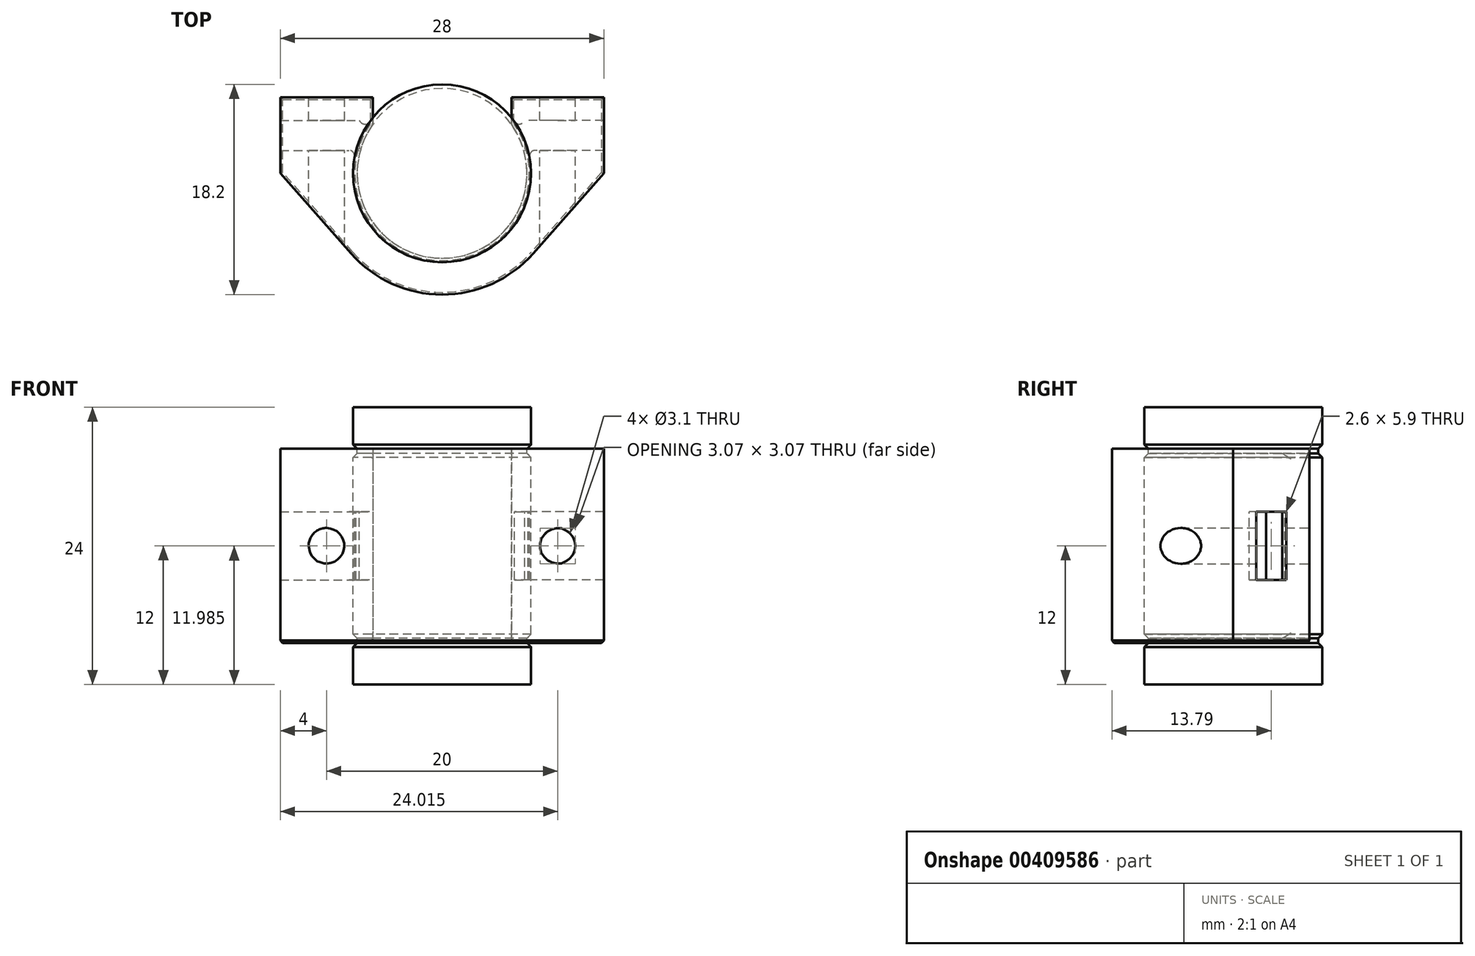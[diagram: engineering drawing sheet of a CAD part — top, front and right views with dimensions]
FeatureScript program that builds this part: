
annotation { "Feature Type Name" : "Feature", "Feature Type Description" : "" }
export const myFeature = defineFeature(function(context is Context, id is Id, definition is map)
    precondition{}
    {
        {
            var Q0;
            Q0=qCreatedBy(makeId("Front.planeOp"),FACE);
            var sketch = newSketch(context, id + "F0", { "sketchPlane" : qUnion([Q0])});
            skLineSegment(sketch, "E0", {"start": v(0, 12) * mm, "end": v(0, -12) * mm});
            skLineSegment(sketch, "E1.bottom", {"start": v(-4, 12) * mm, "end": v(-7.5, 12) * mm});
            skLineSegment(sketch, "E1.top", {"start": v(-4, -12) * mm, "end": v(-7.5, -12) * mm});
            skLineSegment(sketch, "E1.left", {"start": v(-4, 12) * mm, "end": v(-4, -12) * mm, "construction": true});
            skLineSegment(sketch, "E2", {"start": v(-7.5, 12) * mm, "end": v(-7.5, 8.75) * mm, "construction": true});
            skLineSegment(sketch, "E3", {"start": v(-7.5, 8.75) * mm, "end": v(-7.15, 8.75) * mm, "construction": true});
            skLineSegment(sketch, "E4", {"start": v(-7.15, 8.75) * mm, "end": v(-7.15, 7.65) * mm, "construction": true});
            skLineSegment(sketch, "E5", {"start": v(-7.15, 7.65) * mm, "end": v(-7.5, 7.65) * mm, "construction": true});
            skLineSegment(sketch, "E6", {"start": v(-7.5, 7.65) * mm, "end": v(-7.5, 0) * mm, "construction": true});
            skLineSegment(sketch, "E7.MirrorCS", {"start": v(-7.5, -8.75) * mm, "end": v(-7.15, -8.75) * mm, "construction": true});
            skLineSegment(sketch, "E8.MirrorCS", {"start": v(-7.15, -8.75) * mm, "end": v(-7.15, -7.65) * mm, "construction": true});
            skLineSegment(sketch, "E9.MirrorCS", {"start": v(-7.15, -7.65) * mm, "end": v(-7.5, -7.65) * mm, "construction": true});
            skLineSegment(sketch, "E10", {"start": v(-7.5, 0) * mm, "end": v(-7.5, -7.65) * mm, "construction": true});
            skLineSegment(sketch, "E11", {"start": v(-7.5, -8.75) * mm, "end": v(-7.5, -12) * mm, "construction": true});
            skLineSegment(sketch, "E12.0", {"start": v(-7.7, 12) * mm, "end": v(-7.7, 8.75) * mm});
            skLineSegment(sketch, "E13.0", {"start": v(-7.35, 8.75) * mm, "end": v(-7.35, 7.65) * mm});
            skLineSegment(sketch, "E14", {"start": v(-7.7, 8.75) * mm, "end": v(-7.35, 8.4) * mm});
            skLineSegment(sketch, "E15", {"start": v(-7.7, 7.65) * mm, "end": v(-7.7, 0) * mm});
            skLineSegment(sketch, "E16", {"start": v(-7.7, 7.65) * mm, "end": v(-7.35, 8) * mm});
            skLineSegment(sketch, "E17", {"start": v(-7.7, 12) * mm, "end": v(-7.5, 12) * mm});
            skLineSegment(sketch, "E18.MirrorCS", {"start": v(-7.7, -7.65) * mm, "end": v(-7.7, 0) * mm});
            skLineSegment(sketch, "E19.MirrorCS", {"start": v(-7.7, -7.65) * mm, "end": v(-7.35, -8) * mm});
            skLineSegment(sketch, "E20.MirrorCS", {"start": v(-7.35, -8.75) * mm, "end": v(-7.35, -7.65) * mm});
            skLineSegment(sketch, "E21.MirrorCS", {"start": v(-7.7, -8.75) * mm, "end": v(-7.35, -8.4) * mm});
            skLineSegment(sketch, "E22.MirrorCS", {"start": v(-7.7, -12) * mm, "end": v(-7.7, -8.75) * mm});
            skLineSegment(sketch, "E23.MirrorCS", {"start": v(-7.7, -12) * mm, "end": v(-7.5, -12) * mm});
            skLineSegment(sketch, "E24", {"start": v(-4, 12) * mm, "end": v(0, 12) * mm});
            skLineSegment(sketch, "E25", {"start": v(-4, -12) * mm, "end": v(0, -12) * mm});
            skSolve(sketch);
        }
        {
            var Q0;
            Q0=qCreatedBy(makeId("Top.planeOp"),FACE);
            var sketch = newSketch(context, id + "F1", { "sketchPlane" : qUnion([Q0])});
            skLineSegment(sketch, "E26", {"start": v(-5, 6.6) * mm, "end": v(5, 6.6) * mm, "construction": true});
            skCircle(sketch, "E27", {"center": v(0, 0) * mm, "radius": 7.5 * mm, "construction": true});
            skLineSegment(sketch, "E28", {"start": v(5, 6.6) * mm, "end": v(5, 5.6) * mm, "construction": true});
            skLineSegment(sketch, "E29", {"start": v(-5, 6.6) * mm, "end": v(-5, 5.6) * mm, "construction": true});
            skLineSegment(sketch, "E30", {"start": v(-5, 6.6) * mm, "end": v(-10, 6.6) * mm, "construction": true});
            skLineSegment(sketch, "E31", {"start": v(5, 6.6) * mm, "end": v(10, 6.6) * mm, "construction": true});
            skLineSegment(sketch, "E32", {"start": v(-10, 6.6) * mm, "end": v(-10, 4.6) * mm, "construction": true});
            skLineSegment(sketch, "E33.bottom", {"start": v(-12.85, 4.6) * mm, "end": v(-7.15, 4.6) * mm, "construction": true});
            skLineSegment(sketch, "E33.top", {"start": v(-12.85, 2) * mm, "end": v(-7.15, 2) * mm, "construction": true});
            skLineSegment(sketch, "E33.left", {"start": v(-12.85, 4.6) * mm, "end": v(-12.85, 2) * mm, "construction": true});
            skLineSegment(sketch, "E33.right", {"start": v(-7.15, 4.6) * mm, "end": v(-7.15, 2) * mm, "construction": true});
            skSolve(sketch);
        }
        {
            var Q0;
            Q0 = qSketchRegion(id + "F0", true);
            var Q1;
            Q1=sQuery(id+"F0.wireOp",EDGE,"E0");
            revolve(context, id + "F2", {"entities" : qUnion([Q0]), "axis" : qUnion([Q1]), "revolveType" : RevolveType.FULL});
        }
        {
            var Q0;
            Q0=qCreatedBy(makeId("Top.planeOp"),FACE);
            var sketch = newSketch(context, id + "F3", { "sketchPlane" : qUnion([Q0])});
            skPoint(sketch, "E34.0", {"position": v(0, 6.6) * mm});
            skLineSegment(sketch, "E35", {"start": v(0, 6.6) * mm, "end": v(-14, 6.6) * mm, "construction": true});
            skLineSegment(sketch, "E36", {"start": v(-14, 6.6) * mm, "end": v(-14, 0) * mm});
            skLineSegment(sketch, "E37.MirrorCS", {"start": v(0, 6.6) * mm, "end": v(14, 6.6) * mm, "construction": true});
            skLineSegment(sketch, "E38.MirrorCS", {"start": v(14, 6.6) * mm, "end": v(14, 0) * mm});
            skCircle(sketch, "E39.0", {"center": v(0, 0) * mm, "radius": 7.5 * mm, "construction": true});
            skCircle(sketch, "E40.0", {"center": v(0, 0) * mm, "radius": 10.5 * mm, "construction": true});
            skArc(sketch, "E41", {"start": v(-7.88, -6.95) * mm, "mid": v(0, -10.5) * mm, "end": v(7.88, -6.95) * mm});
            skLineSegment(sketch, "E42", {"start": v(-14, 0) * mm, "end": v(-7.87, -6.95) * mm});
            skLineSegment(sketch, "E43.MirrorCS", {"start": v(14, 0) * mm, "end": v(7.87, -6.95) * mm});
            skLineSegment(sketch, "E44.0", {"start": v(-12.85, 4.6) * mm, "end": v(-7.15, 4.6) * mm, "construction": true});
            skLineSegment(sketch, "E45.0", {"start": v(-12.85, 2) * mm, "end": v(-7.15, 2) * mm, "construction": true});
            skLineSegment(sketch, "E46.0", {"start": v(-12.85, 4.6) * mm, "end": v(-12.85, 2) * mm, "construction": true});
            skLineSegment(sketch, "E47", {"start": v(-14, 6.6) * mm, "end": v(-6, 6.6) * mm});
            skLineSegment(sketch, "E48.MirrorCS", {"start": v(14, 6.6) * mm, "end": v(6, 6.6) * mm});
            skLineSegment(sketch, "E49.0", {"start": v(-7.15, 4.6) * mm, "end": v(-7.15, 2) * mm, "construction": true});
            skLineSegment(sketch, "E50", {"start": v(-6, 6.6) * mm, "end": v(-6, 3.3) * mm});
            skPoint(sketch, "E50.endSnap0", {"position": v(-7.15, 3.3) * mm});
            skLineSegment(sketch, "E51", {"start": v(-6, 3.3) * mm, "end": v(0, 3.3) * mm});
            skLineSegment(sketch, "E52.MirrorCS", {"start": v(6, 6.6) * mm, "end": v(6, 3.3) * mm});
            skLineSegment(sketch, "E53.MirrorCS", {"start": v(6, 3.3) * mm, "end": v(0, 3.3) * mm});
            skSolve(sketch);
        }
        {
            var Q0;
            Q0 = qSketchRegion(id + "F3", true);
            var Q1;
            Q1=sQuery(id+"F0.wireOp",VERTEX,"E14.end");
            var Q2;
            Q2=sQuery(id+"F0.wireOp",VERTEX,"E21.MirrorCS.end");
            extrude(context, id + "F4", {"entities" : qUnion([Q0]), "endBound" : BoundingType.UP_TO_VERTEX, "endBoundEntityVertex" : qUnion([Q1]), "depth" : 25 * mm, "hasSecondDirection" : true, "secondDirectionBound" : BoundingType.UP_TO_VERTEX, "secondDirectionOppositeDirection" : true, "secondDirectionBoundEntityVertex" : qUnion([Q2]), "secondDirectionDepth" : 25 * mm});
        }
        {
            var Q0;
            Q0=makeQuery(id+"F4.opExtrude","SWEPT_FACE",FACE,{"disambiguationData":[OSD([sQuery(id+"F3.wireOp",EDGE,"E48.MirrorCS")])]});
            var sketch = newSketch(context, id + "F5", { "sketchPlane" : qUnion([Q0])});
            skPoint(sketch, "E54.0", {"position": v(-10, 0) * mm});
            skPoint(sketch, "E55.0", {"position": v(10, 0) * mm});
            skSolve(sketch);
        }
        {
            var Q0;
            Q0=makeQuery(id+"F2.opRevolve","SWEPT_BODY",BODY,{"disambiguationData":[OSD([sQuery(id+"F0.wireOp",EDGE,"E0"),sQuery(id+"F0.wireOp",EDGE,"E1.bottom"),sQuery(id+"F0.wireOp",EDGE,"E1.top"),sQuery(id+"F0.wireOp",EDGE,"E12.0"),sQuery(id+"F0.wireOp",EDGE,"E13.0"),sQuery(id+"F0.wireOp",EDGE,"E14"),sQuery(id+"F0.wireOp",EDGE,"E15"),sQuery(id+"F0.wireOp",EDGE,"E16"),sQuery(id+"F0.wireOp",EDGE,"E17"),sQuery(id+"F0.wireOp",EDGE,"E18.MirrorCS"),sQuery(id+"F0.wireOp",EDGE,"E19.MirrorCS"),sQuery(id+"F0.wireOp",EDGE,"E20.MirrorCS"),sQuery(id+"F0.wireOp",EDGE,"E21.MirrorCS"),sQuery(id+"F0.wireOp",EDGE,"E22.MirrorCS"),sQuery(id+"F0.wireOp",EDGE,"E23.MirrorCS"),sQuery(id+"F0.wireOp",EDGE,"E24"),sQuery(id+"F0.wireOp",EDGE,"E25")])]});
            var Q1;
            Q1=makeQuery(id+"F4.opExtrude","SWEPT_BODY",BODY,{"disambiguationData":[OSD([sQuery(id+"F3.wireOp",EDGE,"E36"),sQuery(id+"F3.wireOp",EDGE,"E38.MirrorCS"),sQuery(id+"F3.wireOp",EDGE,"E41"),sQuery(id+"F3.wireOp",EDGE,"E42"),sQuery(id+"F3.wireOp",EDGE,"E43.MirrorCS"),sQuery(id+"F3.wireOp",EDGE,"E47"),sQuery(id+"F3.wireOp",EDGE,"E48.MirrorCS"),sQuery(id+"F3.wireOp",EDGE,"E50"),sQuery(id+"F3.wireOp",EDGE,"E51"),sQuery(id+"F3.wireOp",EDGE,"E52.MirrorCS"),sQuery(id+"F3.wireOp",EDGE,"E53.MirrorCS")])]});
            booleanBodies(context, id + "F6", {"operationType" : BooleanOperationType.SUBTRACTION, "tools" : qUnion([Q0]), "targets" : qUnion([Q1]), "keepTools" : true});
        }
        {
            var Q0;
            Q0=sQuery(id+"F5.wireOp",VERTEX,"E54.0");
            var Q1;
            Q1=sQuery(id+"F5.wireOp",VERTEX,"E55.0");
            var Q2;
            Q2=makeQuery(id+"F4.opExtrude","SWEPT_BODY",BODY,{"disambiguationData":[OSD([sQuery(id+"F3.wireOp",EDGE,"E36"),sQuery(id+"F3.wireOp",EDGE,"E38.MirrorCS"),sQuery(id+"F3.wireOp",EDGE,"E41"),sQuery(id+"F3.wireOp",EDGE,"E42"),sQuery(id+"F3.wireOp",EDGE,"E43.MirrorCS"),sQuery(id+"F3.wireOp",EDGE,"E47"),sQuery(id+"F3.wireOp",EDGE,"E48.MirrorCS"),sQuery(id+"F3.wireOp",EDGE,"E50"),sQuery(id+"F3.wireOp",EDGE,"E51"),sQuery(id+"F3.wireOp",EDGE,"E52.MirrorCS"),sQuery(id+"F3.wireOp",EDGE,"E53.MirrorCS")])]});
            hole(context, id + "F7", {"style" : HoleStyle.SIMPLE, "endStyle" : HoleEndStyle.THROUGH, "holeDiameter" : 3.1 * mm, "isTappedThrough" : true, "tappedDepth" : 12 * mm, "tapClearance" : 3, "locations" : qUnion([Q0, Q1]), "scope" : qUnion([Q2])});
        }
        {
            var Q0;
            Q0=qCreatedBy(makeId("Top.planeOp"),FACE);
            var sketch = newSketch(context, id + "F8", { "sketchPlane" : qUnion([Q0])});
            skLineSegment(sketch, "E56.0", {"start": v(-12.85, 2) * mm, "end": v(-7.15, 2) * mm});
            skLineSegment(sketch, "E57.0", {"start": v(-12.85, 4.6) * mm, "end": v(-12.85, 2) * mm, "construction": true});
            skLineSegment(sketch, "E58.0", {"start": v(-12.85, 4.6) * mm, "end": v(-7.15, 4.6) * mm});
            skLineSegment(sketch, "E59.0", {"start": v(-7.15, 4.6) * mm, "end": v(-7.15, 2) * mm});
            skLineSegment(sketch, "E60.MirrorCS", {"start": v(12.85, 4.6) * mm, "end": v(7.15, 4.6) * mm});
            skLineSegment(sketch, "E61.MirrorCS", {"start": v(12.85, 4.6) * mm, "end": v(12.85, 2) * mm, "construction": true});
            skLineSegment(sketch, "E62.MirrorCS", {"start": v(12.85, 2) * mm, "end": v(7.15, 2) * mm});
            skLineSegment(sketch, "E63.MirrorCS", {"start": v(7.15, 4.6) * mm, "end": v(7.15, 2) * mm});
            skLineSegment(sketch, "E64", {"start": v(-12.85, 4.6) * mm, "end": v(-19.02, 4.6) * mm});
            skLineSegment(sketch, "E65", {"start": v(-19.02, 4.6) * mm, "end": v(-19.02, 2) * mm});
            skLineSegment(sketch, "E66", {"start": v(-19.02, 2) * mm, "end": v(-12.85, 2) * mm});
            skLineSegment(sketch, "E67.MirrorCS", {"start": v(12.85, 4.6) * mm, "end": v(19.02, 4.6) * mm});
            skLineSegment(sketch, "E68.MirrorCS", {"start": v(19.02, 4.6) * mm, "end": v(19.02, 2) * mm});
            skLineSegment(sketch, "E69.MirrorCS", {"start": v(19.02, 2) * mm, "end": v(12.85, 2) * mm});
            skSolve(sketch);
        }
        {
            var Q0;
            Q0 = qSketchRegion(id + "F8", true);
            extrude(context, id + "F9", {"entities" : qUnion([Q0]), "operationType" : NewBodyOperationType.REMOVE, "depth" : (0.4 + 5.5) * mm, "symmetric" : true});
        }
        {
            var Q0;
            Q0=makeQuery(id+"F4.opExtrude","TWEAK_EDGE",EDGE,{"derivedFrom":[makeQuery(id+"F3.imprint","IMPRINT",EDGE,{"derivedFrom":sQuery(id+"F3.wireOp",EDGE,"E47")}),makeQuery(id+"F3.imprint","IMPRINT",EDGE,{"derivedFrom":sQuery(id+"F3.wireOp",EDGE,"E50")})]});
            var Q1;
            Q1=makeQuery(id+"F4.opExtrude","TWEAK_EDGE",EDGE,{"derivedFrom":[makeQuery(id+"F3.imprint","IMPRINT",EDGE,{"derivedFrom":sQuery(id+"F3.wireOp",EDGE,"E36")}),makeQuery(id+"F3.imprint","IMPRINT",EDGE,{"derivedFrom":sQuery(id+"F3.wireOp",EDGE,"E47")})]});
            var Q2;
            Q2=makeQuery(id+"F4.opExtrude","TWEAK_EDGE",EDGE,{"derivedFrom":[makeQuery(id+"F3.imprint","IMPRINT",EDGE,{"derivedFrom":sQuery(id+"F3.wireOp",EDGE,"E48.MirrorCS")}),makeQuery(id+"F3.imprint","IMPRINT",EDGE,{"derivedFrom":sQuery(id+"F3.wireOp",EDGE,"E52.MirrorCS")})]});
            var Q3;
            Q3=makeQuery(id+"F4.opExtrude","TWEAK_EDGE",EDGE,{"derivedFrom":[makeQuery(id+"F3.imprint","IMPRINT",EDGE,{"derivedFrom":sQuery(id+"F3.wireOp",EDGE,"E38.MirrorCS")}),makeQuery(id+"F3.imprint","IMPRINT",EDGE,{"derivedFrom":sQuery(id+"F3.wireOp",EDGE,"E48.MirrorCS")})]});
            var Q4;
            Q4=makeQuery(id+"F6.opBoolean","INTERSECT",EDGE,{"derivedFrom":[makeQuery(id+"F2.opRevolve","SWEPT_FACE",FACE,{"disambiguationData":[OSD([sQuery(id+"F0.wireOp",EDGE,"E15"),sQuery(id+"F0.wireOp",EDGE,"E18.MirrorCS")])]}),makeQuery(id+"F4.opExtrude","SWEPT_FACE",FACE,{"disambiguationData":[OSD([sQuery(id+"F3.wireOp",EDGE,"E52.MirrorCS")])]})]});
            var Q5;
            Q5=makeQuery(id+"F6.opBoolean","INTERSECT",EDGE,{"derivedFrom":[makeQuery(id+"F2.opRevolve","SWEPT_FACE",FACE,{"disambiguationData":[OSD([sQuery(id+"F0.wireOp",EDGE,"E15"),sQuery(id+"F0.wireOp",EDGE,"E18.MirrorCS")])]}),makeQuery(id+"F4.opExtrude","SWEPT_FACE",FACE,{"disambiguationData":[OSD([sQuery(id+"F3.wireOp",EDGE,"E50")])]})]});
            var Q6;
            Q6=makeQuery(id+"F6.opBoolean","INTERSECT",EDGE,{"derivedFrom":[makeQuery(id+"F2.opRevolve","SWEPT_FACE",FACE,{"disambiguationData":[OSD([sQuery(id+"F0.wireOp",EDGE,"E13.0")])]}),makeQuery(id+"F4.opExtrude","SWEPT_FACE",FACE,{"disambiguationData":[OSD([sQuery(id+"F3.wireOp",EDGE,"E50")])]})]});
            var Q7;
            Q7=makeQuery(id+"F6.opBoolean","INTERSECT",EDGE,{"derivedFrom":[makeQuery(id+"F2.opRevolve","SWEPT_FACE",FACE,{"disambiguationData":[OSD([sQuery(id+"F0.wireOp",EDGE,"E20.MirrorCS")])]}),makeQuery(id+"F4.opExtrude","SWEPT_FACE",FACE,{"disambiguationData":[OSD([sQuery(id+"F3.wireOp",EDGE,"E50")])]})]});
            var Q8;
            Q8=makeQuery(id+"F6.opBoolean","INTERSECT",EDGE,{"derivedFrom":[makeQuery(id+"F2.opRevolve","SWEPT_FACE",FACE,{"disambiguationData":[OSD([sQuery(id+"F0.wireOp",EDGE,"E13.0")])]}),makeQuery(id+"F4.opExtrude","SWEPT_FACE",FACE,{"disambiguationData":[OSD([sQuery(id+"F3.wireOp",EDGE,"E52.MirrorCS")])]})]});
            var Q9;
            Q9=makeQuery(id+"F6.opBoolean","INTERSECT",EDGE,{"derivedFrom":[makeQuery(id+"F2.opRevolve","SWEPT_FACE",FACE,{"disambiguationData":[OSD([sQuery(id+"F0.wireOp",EDGE,"E20.MirrorCS")])]}),makeQuery(id+"F4.opExtrude","SWEPT_FACE",FACE,{"disambiguationData":[OSD([sQuery(id+"F3.wireOp",EDGE,"E52.MirrorCS")])]})]});
            var Q10;
            Q10=makeQuery(id+"F4.opExtrude","TWEAK_EDGE",EDGE,{"derivedFrom":[makeQuery(id+"F3.imprint","IMPRINT",EDGE,{"derivedFrom":sQuery(id+"F3.wireOp",EDGE,"E36")}),makeQuery(id+"F3.imprint","IMPRINT",EDGE,{"derivedFrom":sQuery(id+"F3.wireOp",EDGE,"E42")})]});
            var Q11;
            Q11=makeQuery(id+"F4.opExtrude","TWEAK_EDGE",EDGE,{"derivedFrom":[makeQuery(id+"F3.imprint","IMPRINT",EDGE,{"derivedFrom":sQuery(id+"F3.wireOp",EDGE,"E38.MirrorCS")}),makeQuery(id+"F3.imprint","IMPRINT",EDGE,{"derivedFrom":sQuery(id+"F3.wireOp",EDGE,"E43.MirrorCS")})]});
            var Q12;
            Q12=makeQuery(id+"F9.boolean.opBoolean","INTERSECT",EDGE,{"derivedFrom":[makeQuery(id+"F6.opBoolean","COPY",FACE,{"derivedFrom":makeQuery(id+"F2.opRevolve","SWEPT_FACE",FACE,{"disambiguationData":[OSD([sQuery(id+"F0.wireOp",EDGE,"E15"),sQuery(id+"F0.wireOp",EDGE,"E18.MirrorCS")])]})}),makeQuery(id+"F9.opExtrude","SWEPT_FACE",FACE,{"disambiguationData":[OSD([sQuery(id+"F8.wireOp",EDGE,"E59.0")])]})]});
            var Q13;
            Q13=makeQuery(id+"F9.boolean.opBoolean","INTERSECT",EDGE,{"derivedFrom":[makeQuery(id+"F6.opBoolean","COPY",FACE,{"derivedFrom":makeQuery(id+"F2.opRevolve","SWEPT_FACE",FACE,{"disambiguationData":[OSD([sQuery(id+"F0.wireOp",EDGE,"E15"),sQuery(id+"F0.wireOp",EDGE,"E18.MirrorCS")])]})}),makeQuery(id+"F9.opExtrude","SWEPT_FACE",FACE,{"disambiguationData":[OSD([sQuery(id+"F8.wireOp",EDGE,"E63.MirrorCS")])]})]});
            var Q14;
            Q14=makeQuery(id+"F9.boolean.opBoolean","INTERSECT",EDGE,{"derivedFrom":[makeQuery(id+"F6.opBoolean","COPY",FACE,{"derivedFrom":makeQuery(id+"F2.opRevolve","SWEPT_FACE",FACE,{"disambiguationData":[OSD([sQuery(id+"F0.wireOp",EDGE,"E15"),sQuery(id+"F0.wireOp",EDGE,"E18.MirrorCS")])]})}),makeQuery(id+"F9.opExtrude","SWEPT_FACE",FACE,{"disambiguationData":[OSD([sQuery(id+"F8.wireOp",EDGE,"E56.0"),sQuery(id+"F8.wireOp",EDGE,"E66")])]})]});
            var Q15;
            Q15=makeQuery(id+"F9.boolean.opBoolean","INTERSECT",EDGE,{"derivedFrom":[makeQuery(id+"F6.opBoolean","COPY",FACE,{"derivedFrom":makeQuery(id+"F2.opRevolve","SWEPT_FACE",FACE,{"disambiguationData":[OSD([sQuery(id+"F0.wireOp",EDGE,"E15"),sQuery(id+"F0.wireOp",EDGE,"E18.MirrorCS")])]})}),makeQuery(id+"F9.opExtrude","SWEPT_FACE",FACE,{"disambiguationData":[OSD([sQuery(id+"F8.wireOp",EDGE,"E62.MirrorCS"),sQuery(id+"F8.wireOp",EDGE,"E69.MirrorCS")])]})]});
            fillet(context, id + "F10", {"entities" : qUnion([Q0, Q1, Q2, Q3, Q4, Q5, Q6, Q7, Q8, Q9, Q10, Q11, Q12, Q13, Q14, Q15]), "radius" : .5 * mm, "allowEdgeOverflow" : false});
        }
        {
            var Q0;
            Q0=makeQuery(id+"F4.opExtrude","CAP_FACE",FACE,{"disambiguationData":[OSD([sQuery(id+"F3.wireOp",EDGE,"E36"),sQuery(id+"F3.wireOp",EDGE,"E38.MirrorCS"),sQuery(id+"F3.wireOp",EDGE,"E41"),sQuery(id+"F3.wireOp",EDGE,"E42"),sQuery(id+"F3.wireOp",EDGE,"E43.MirrorCS"),sQuery(id+"F3.wireOp",EDGE,"E47"),sQuery(id+"F3.wireOp",EDGE,"E48.MirrorCS"),sQuery(id+"F3.wireOp",EDGE,"E50"),sQuery(id+"F3.wireOp",EDGE,"E51"),sQuery(id+"F3.wireOp",EDGE,"E52.MirrorCS"),sQuery(id+"F3.wireOp",EDGE,"E53.MirrorCS")])],"isStart":true});
            chamfer(context, id + "F11", {"entities" : qUnion([Q0]), "width" : .2 * mm});
        }
    });
